# Revit family: NBS_Schluter-SystemsLtd_WstesForShwrTrys_Schluter-KERDI-LINE-H50
name_source: partatom
category: Plumbing Fixtures
revit_build: Autodesk Revit 2015 (Build: 20140606_1530(x64)
units: mm (PartAtom-declared; Revit-internal decimal feet)

## types (1)
- 500mm_DesignerGrate_A
    AssetType = Fixed
    BIMObjectName = NBS_Schlüter-SystemsLtd_WastesForShowerTrays_Schlüter®-KERDI-LINE-H50-500mm
    BodyMaterial = Channel body: Stainless steel V4A 1.4404; Drain body: High impact polypropylene (PP); Odour trap: Acrylonitrile butadiene styrene (ABS); Frame: Stainless steel V4A 1.440; Channel support: Pressure resistant, expanded polystyrene (EPS)
    Category = Pr_70_55_96_83:Shower tray wastes
    ChannelSupportHeight = 97 mm  [stored 0.318241 ft]
    ChannelSupportLength = 519.4 mm
    ChannelSupportMaterial = NBS_Concept
    Color = white and grey
    CoverLength = 523.4 mm
    CoverMaterial = Stainless steel V4A 1.440
    CoverWidth = 74 mm
    Depth = 110.7 mm  [stored 0.363189 ft]
    Description = Horizontal drain with integrated odour trap
    DesignerGrate = NBS_Schluter-SystemsLtd_WstesForShwrTrys_KERDI-LINE_Grate_A
    DrainageCapacity = DN 50 = 0.6 L/s (36 L/min)
    DurationUnit = year
    Features = Pre-adhered waterproof collor made of Schlüter®-KERDI to ensure reliable connection between channel body and the floor and/or wall.
    Form = Flush linear drain
    FrameHeightOptions = 19 mm (for coverings with thicknesses of 3-15 mm), 30 mm (for coverings with thicknesses of 13-25 mm)
    GrateOptions = Designer Grate A, Designer Grate B, Designer Grate C, Designer Grate D
    IfcExportAs = IfcWasteTerminalType
    IfcExportType = FLOORWASTE
    Length = 550 mm
    Manufacturer = www.schluter.co.uk
    ManufacturerName = Schlüter-Systems Ltd
    ManufacturerURL = www.schluter.co.uk
    ModelNumber = KLH 50 GE 50
    ModelReference = Schlüter®-KERDI-LINE-H 50
    NBSCertification = www.nationalbimlibrary.com/cert/glylpsy5
    NBSDescription = Wastes for shower trays
    NBSReference = 45-35-70/337
    Name = WastesForShowerTrays_Schlüter®-KERDI-LINE-H50_500mm_Schlüter-SystemsLtd
    NominalBodyDepth = 0 mm  [stored 0 ft]
    NominalBodyLength = 550 mm
    NominalBodyWidth = 0 mm  [stored 0 ft]
    NominalHeight = 97 mm  [stored 0.318241 ft]
    NominalLength = 500 mm  [stored 1.64042 ft]
    NominalWidth = 0 mm  [stored 0 ft]
    OutletConnectionSize = 50 mm  [stored 0.164042 ft]
    ProductInformation = www.schluter.co.uk<userpath>
    ShowerTrayGrateMaterial = NBS_Concept
    SuitableFrameCoverings = Ceramic tiles, natural stone and other coatings
    Uniclass2015Code = Pr_70_55_96_83
    Uniclass2015Title = Shower tray wastes
    Uniclass2015Version = Products v1.5
    Version = 2
    WarrantyDescription = 5 years (Please contact Schlüter-Systems for further warranty information)
    WarrantyDurationUnit = year
    Width = 137 mm  [stored 0.449475 ft]

note: [stored X ft] marks values corroborated as IEEE doubles in the binary element streams (Revit-internal decimal feet)

## geometry (parser evidence)
native form markers: Sweep x23
no freeform markers — native parametric forms only
